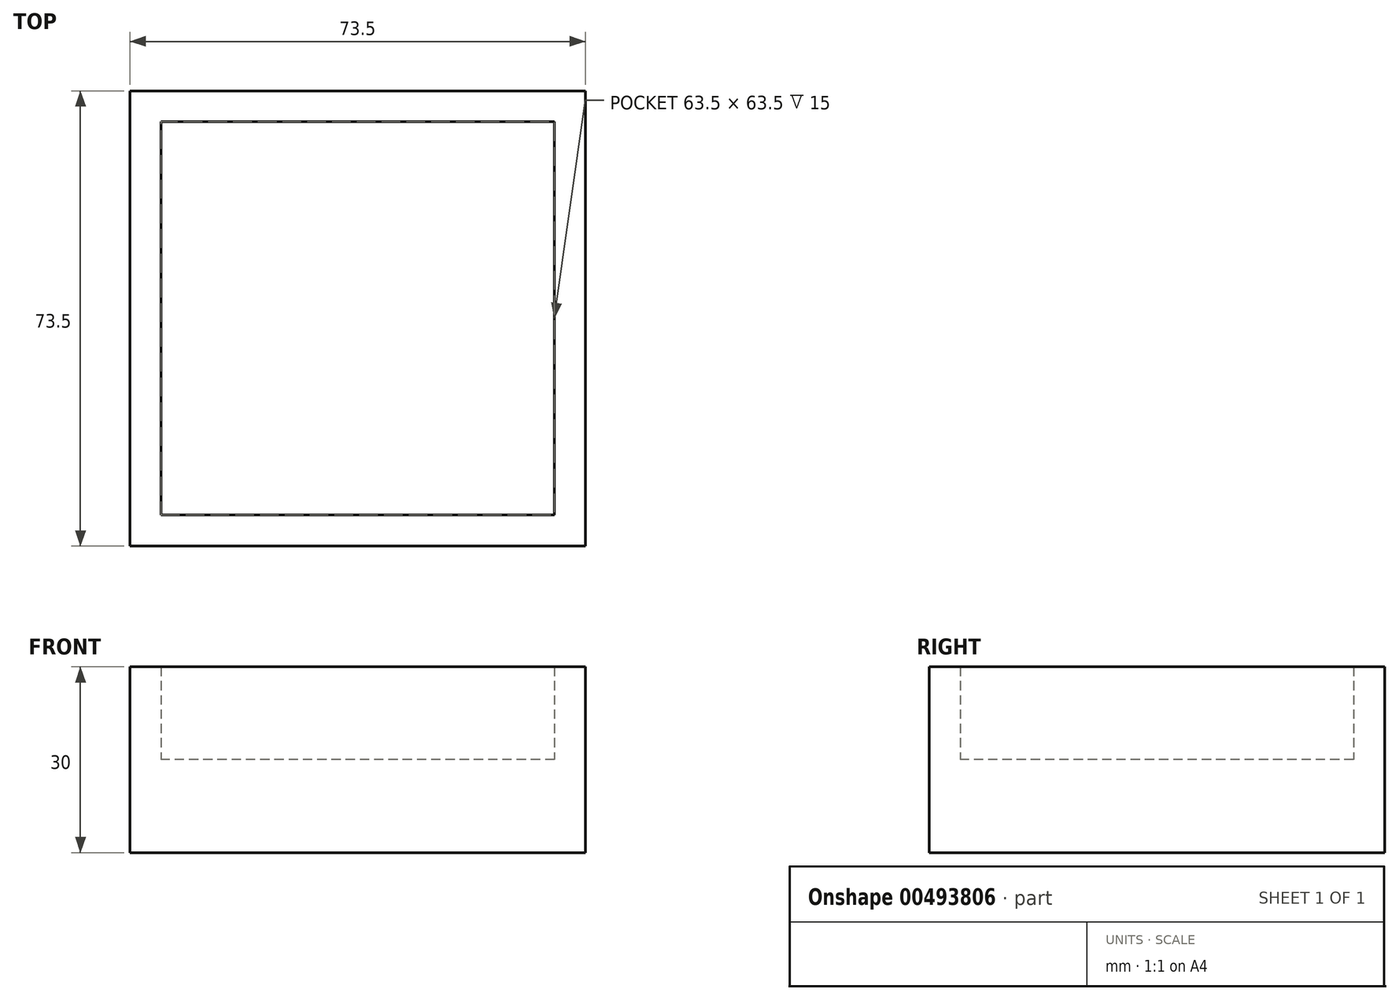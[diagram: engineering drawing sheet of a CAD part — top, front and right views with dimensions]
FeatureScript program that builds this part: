
annotation { "Feature Type Name" : "Feature", "Feature Type Description" : "" }
export const myFeature = defineFeature(function(context is Context, id is Id, definition is map)
    precondition{}
    {
        {
            var Q0;
            Q0=qCreatedBy(makeId("Top.planeOp"),FACE);
            var sketch = newSketch(context, id + "F0", { "sketchPlane" : qUnion([Q0])});
            skLineSegment(sketch, "E0.bottom", {"start": v(31.75, 31.75) * mm, "end": v(-31.75, 31.75) * mm});
            skLineSegment(sketch, "E0.top", {"start": v(31.75, -31.75) * mm, "end": v(-31.75, -31.75) * mm});
            skLineSegment(sketch, "E0.left", {"start": v(31.75, 31.75) * mm, "end": v(31.75, -31.75) * mm});
            skLineSegment(sketch, "E0.right", {"start": v(-31.75, 31.75) * mm, "end": v(-31.75, -31.75) * mm});
            skPoint(sketch, "E0.middle", {"position": v(0, 0) * mm});
            skLineSegment(sketch, "E1.0", {"start": v(36.75, 36.75) * mm, "end": v(-36.75, 36.75) * mm});
            skLineSegment(sketch, "E1.1", {"start": v(36.75, 36.75) * mm, "end": v(36.75, -36.75) * mm});
            skLineSegment(sketch, "E1.2", {"start": v(36.75, -36.75) * mm, "end": v(-36.75, -36.75) * mm});
            skLineSegment(sketch, "E1.3", {"start": v(-36.75, 36.75) * mm, "end": v(-36.75, -36.75) * mm});
            skSolve(sketch);
        }
        {
            var Q0;
            Q0=makeQuery(id+"F0.imprint","IMPRINT",FACE,{"disambiguationData":[TD([[makeQuery(id+"F0.imprint","IMPRINT",EDGE,{"derivedFrom":sQuery(id+"F0.wireOp",EDGE,"E0.bottom")}),1.0]])]});
            extrude(context, id + "F1", {"entities" : qUnion([Q0]), "depth" : 15 * mm, "offsetDistance" : 25 * mm});
        }
        {
            var Q0;
            Q0=qSketchRegion(id+"F0",true);
            extrude(context, id + "F2", {"entities" : qUnion([Q0]), "operationType" : NewBodyOperationType.ADD, "depth" : 30 * mm, "offsetDistance" : 25 * mm});
        }
    });
